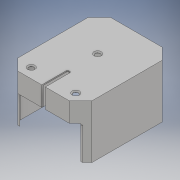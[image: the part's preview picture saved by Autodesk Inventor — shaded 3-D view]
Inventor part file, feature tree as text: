
AUTODESK INVENTOR PART (.ipt)
format: ipt  version: 2017 (Build 210142000, 142)  size: 250,368 bytes
history: native  units: mm
features: extrude x8, sketch x6, other x5, fillet x4, hole x3
ambient origin geometry x8: Origin, YZ Plane, XZ Plane, XY Plane, X Axis, Y Axis, Z Axis, Center Point
bodies: Body1 (feature_tree)
feature tree (26):
  other  "Твердое тело1"
  sketch  "Эскиз1"
  extrude  "Выдавливание1"  Depth=58.6mm
  extrude  "Выдавливание2"  Depth=74.0mm
  fillet  "Сопряжение1"  Radius=8.5mm
  extrude  "Выдавливание3"  Depth=8.5mm
  extrude  "Выдавливание4"  Depth=8.5mm
  extrude  "Выдавливание5"  Depth=8.5mm
  other  "Комбинировать1"
  hole  "Отверстие4"  [1 undecoded]
  hole  "Отверстие5"  [1 undecoded]
  hole  "Отверстие6"  [1 undecoded]
  fillet  "Сопряжение2"  Radius=8.5mm
  fillet  "Сопряжение3"  Radius=1.2mm
  extrude  "Выдавливание6"  Depth=1.0mm TaperAngle=0.0deg
  extrude  "Выдавливание7"  Depth=43.0mm TaperAngle=0.0deg
  extrude  "Выдавливание8"  Depth=1.0mm
  other  "Комбинировать2"
  fillet  "Сопряжение4"  Radius=3.0mm
  other  "Твердое тело2"
  sketch  "Эскиз2"
  sketch  "Эскиз3"
  sketch  "Эскиз4"
  other  "Твердое тело3"
  sketch  "Эскиз5"
  sketch  "Эскиз6"
note: 3 required parameter values undecoded (feature->parameter linkage not recoverable at this tier; creation-order binding heuristic only, values carry confidence <= 0.55)
